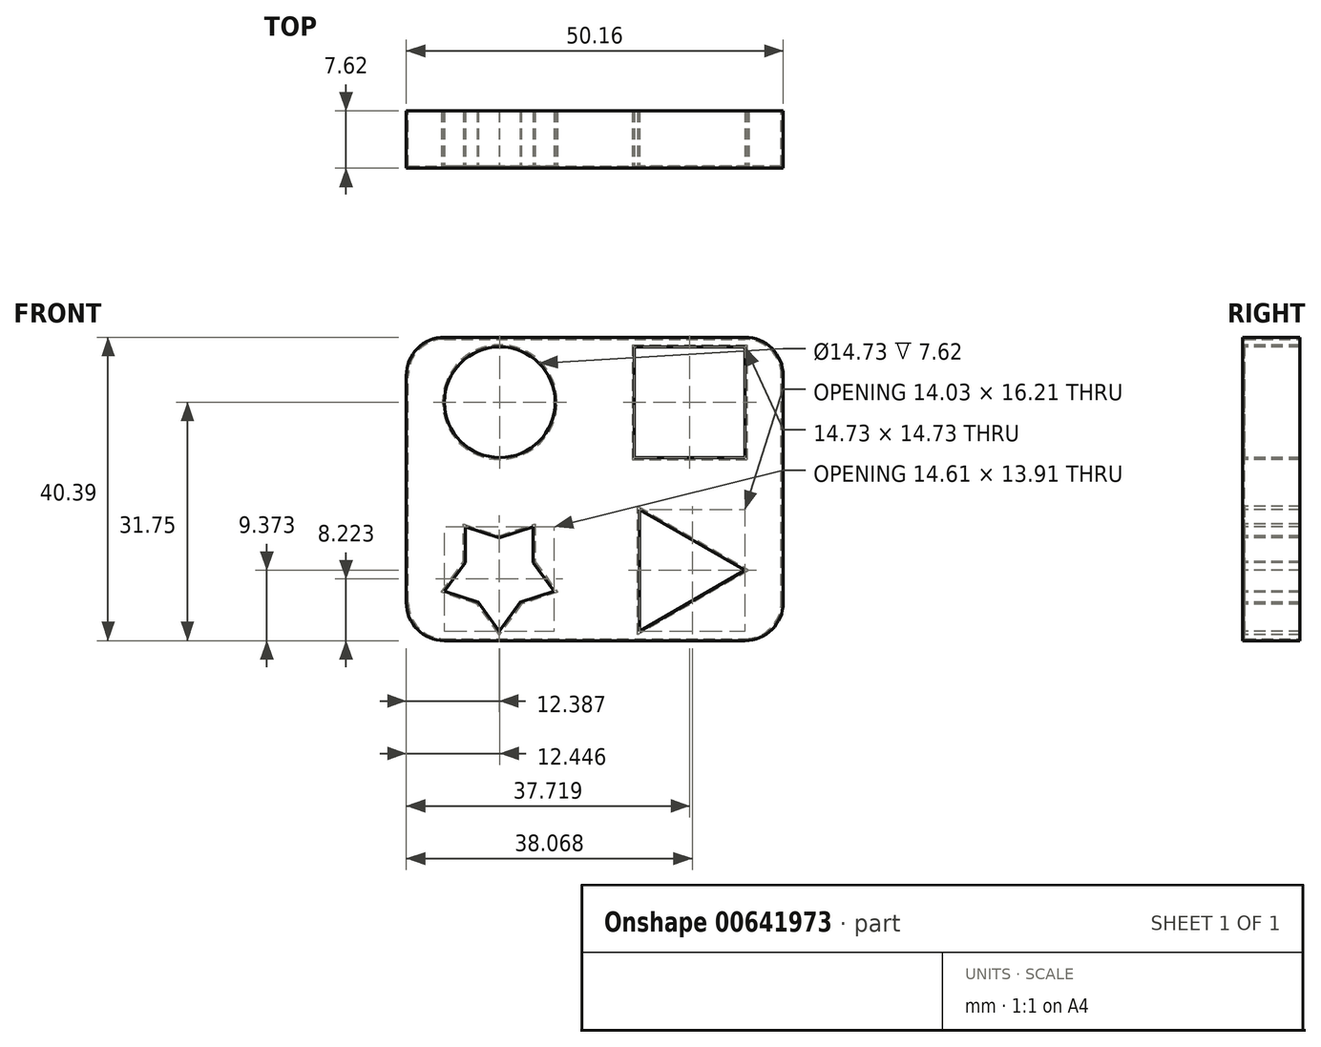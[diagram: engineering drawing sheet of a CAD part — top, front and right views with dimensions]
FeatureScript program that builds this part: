
annotation { "Feature Type Name" : "Feature", "Feature Type Description" : "" }
export const myFeature = defineFeature(function(context is Context, id is Id, definition is map)
    precondition{}
    {
        {
            var Q0;
            Q0=qCreatedBy(makeId("Front.planeOp"),FACE);
            var sketch = newSketch(context, id + "F0", { "sketchPlane" : qUnion([Q0])});
            skLineSegment(sketch, "E0.bottom", {"start": v(5.08, 0) * mm, "end": v(45.09, 0) * mm});
            skLineSegment(sketch, "E0.top", {"start": v(5.08, 40.39) * mm, "end": v(45.09, 40.39) * mm});
            skLineSegment(sketch, "E0.left", {"start": v(0, 5.08) * mm, "end": v(0, 35.3) * mm});
            skLineSegment(sketch, "E0.right", {"start": v(50.16, 5.08) * mm, "end": v(50.16, 35.3) * mm});
            skPoint(sketch, "E1.visualSharp", {"position": v(50.16, 40.39) * mm});
            skArc(sketch, "E1.filletArc", {"start": v(50.16, 35.3) * mm, "mid": v(48.68, 38.9) * mm, "end": v(45.09, 40.39) * mm});
            skPoint(sketch, "E2.visualSharp", {"position": v(0, 40.39) * mm});
            skArc(sketch, "E2.filletArc", {"start": v(5.08, 40.39) * mm, "mid": v(1.49, 38.9) * mm, "end": v(0, 35.3) * mm});
            skPoint(sketch, "E3.visualSharp", {"position": v(0, 0) * mm});
            skArc(sketch, "E3.filletArc", {"start": v(0, 5.08) * mm, "mid": v(1.49, 1.49) * mm, "end": v(5.08, 0) * mm});
            skPoint(sketch, "E4.visualSharp", {"position": v(50.17, 0) * mm});
            skArc(sketch, "E4.filletArc", {"start": v(45.09, 0) * mm, "mid": v(48.68, 1.49) * mm, "end": v(50.16, 5.08) * mm});
            skSolve(sketch);
        }
        {
            var Q0;
            Q0=makeQuery(id+"F0.imprint","IMPRINT",FACE,{"disambiguationData":[TD([[makeQuery(id+"F0.imprint","IMPRINT",EDGE,{"derivedFrom":sQuery(id+"F0.wireOp",EDGE,"E0.bottom")}),1.0]])]});
            extrude(context, id + "F1", {"entities" : qUnion([Q0]), "depth" : 7.62 * mm, "offsetDistance" : 25.4 * mm});
        }
        {
            var Q0;
            Q0=makeQuery(id+"F1.opExtrude","CAP_FACE",FACE,{"disambiguationData":[OSD([sQuery(id+"F0.wireOp",EDGE,"E0.bottom"),sQuery(id+"F0.wireOp",EDGE,"E0.top"),sQuery(id+"F0.wireOp",EDGE,"E0.left"),sQuery(id+"F0.wireOp",EDGE,"E0.right"),sQuery(id+"F0.wireOp",EDGE,"E1.filletArc"),sQuery(id+"F0.wireOp",EDGE,"E2.filletArc"),sQuery(id+"F0.wireOp",EDGE,"E3.filletArc"),sQuery(id+"F0.wireOp",EDGE,"E4.filletArc")])],"isStart":false});
            var sketch = newSketch(context, id + "F2", { "sketchPlane" : qUnion([Q0])});
            skLineSegment(sketch, "E5.bottom", {"start": v(30.35, 39.12) * mm, "end": v(45.09, 39.12) * mm});
            skLineSegment(sketch, "E5.top", {"start": v(30.35, 24.38) * mm, "end": v(45.09, 24.38) * mm});
            skLineSegment(sketch, "E5.left", {"start": v(30.35, 39.12) * mm, "end": v(30.35, 24.38) * mm});
            skLineSegment(sketch, "E5.right", {"start": v(45.09, 39.12) * mm, "end": v(45.09, 24.38) * mm});
            skSolve(sketch);
        }
        {
            var Q0;
            Q0=makeQuery(id+"F2.imprint","IMPRINT",FACE,{"disambiguationData":[TD([[makeQuery(id+"F2.imprint","IMPRINT",EDGE,{"derivedFrom":sQuery(id+"F2.wireOp",EDGE,"E5.bottom")}),1.0]])]});
            var sketch = newSketch(context, id + "F3", { "sketchPlane" : qUnion([Q0])});
            skLineSegment(sketch, "E6", {"start": v(31.05, 1.27) * mm, "end": v(31.05, 17.48) * mm});
            skLineSegment(sketch, "E7", {"start": v(31.05, 17.48) * mm, "end": v(45.09, 9.37) * mm});
            skLineSegment(sketch, "E8", {"start": v(45.09, 9.37) * mm, "end": v(31.05, 1.27) * mm});
            skSolve(sketch);
        }
        {
            var Q0;
            Q0=makeQuery(id+"F2.imprint","IMPRINT",FACE,{"disambiguationData":[TD([[makeQuery(id+"F2.imprint","IMPRINT",EDGE,{"derivedFrom":sQuery(id+"F2.wireOp",EDGE,"E5.bottom")}),1.0]])]});
            var sketch = newSketch(context, id + "F4", { "sketchPlane" : qUnion([Q0])});
            skCircle(sketch, "E9.cCircle", {"center": v(12.38, 8.95) * mm, "radius": 7.68 * mm, "construction": true});
            skLineSegment(sketch, "E9.0", {"start": v(12.4, 1.27) * mm, "end": v(5.08, 6.57) * mm});
            skLineSegment(sketch, "E9.1", {"start": v(5.08, 6.57) * mm, "end": v(7.86, 15.16) * mm});
            skLineSegment(sketch, "E9.2", {"start": v(7.86, 15.16) * mm, "end": v(16.9, 15.18) * mm});
            skLineSegment(sketch, "E9.3", {"start": v(16.9, 15.18) * mm, "end": v(19.7, 6.59) * mm});
            skLineSegment(sketch, "E9.4", {"start": v(19.7, 6.59) * mm, "end": v(12.4, 1.27) * mm});
            skLineSegment(sketch, "E10", {"start": v(16.9, 15.18) * mm, "end": v(16.9, 10.43) * mm});
            skLineSegment(sketch, "E11", {"start": v(16.9, 10.43) * mm, "end": v(19.7, 6.59) * mm});
            skLineSegment(sketch, "E12", {"start": v(19.7, 6.59) * mm, "end": v(15.16, 5.1) * mm});
            skLineSegment(sketch, "E13", {"start": v(15.16, 5.1) * mm, "end": v(12.4, 1.27) * mm});
            skLineSegment(sketch, "E14", {"start": v(12.4, 1.27) * mm, "end": v(9.6, 5.1) * mm});
            skLineSegment(sketch, "E15", {"start": v(9.6, 5.1) * mm, "end": v(5.08, 6.57) * mm});
            skLineSegment(sketch, "E16", {"start": v(5.08, 6.57) * mm, "end": v(7.87, 10.41) * mm});
            skLineSegment(sketch, "E17", {"start": v(7.87, 10.41) * mm, "end": v(7.86, 15.16) * mm});
            skLineSegment(sketch, "E18", {"start": v(7.86, 15.16) * mm, "end": v(12.38, 13.7) * mm});
            skLineSegment(sketch, "E19", {"start": v(12.38, 13.7) * mm, "end": v(16.9, 15.18) * mm});
            skSolve(sketch);
        }
        {
            var Q0;
            Q0=makeQuery(id+"F2.imprint","IMPRINT",FACE,{"disambiguationData":[TD([[makeQuery(id+"F2.imprint","IMPRINT",EDGE,{"derivedFrom":sQuery(id+"F2.wireOp",EDGE,"E5.bottom")}),-1.0]])]});
            extrude(context, id + "F5", {"entities" : qUnion([Q0]), "operationType" : NewBodyOperationType.REMOVE, "oppositeDirection" : true, "depth" : 25.4 * mm, "offsetDistance" : 25.4 * mm});
        }
        {
            var Q0;
            Q0=makeQuery(id+"F3.imprint","IMPRINT",FACE,{"disambiguationData":[TD([[makeQuery(id+"F3.imprint","IMPRINT",EDGE,{"derivedFrom":sQuery(id+"F3.wireOp",EDGE,"E6")}),-1.0]])]});
            extrude(context, id + "F6", {"entities" : qUnion([Q0]), "operationType" : NewBodyOperationType.REMOVE, "oppositeDirection" : true, "depth" : 25.4 * mm, "offsetDistance" : 25.4 * mm});
        }
        {
            var Q0;
            Q0=makeQuery(id+"F4.imprint","IMPRINT",FACE,{"disambiguationData":[TD([[makeQuery(id+"F4.imprint","IMPRINT",EDGE,{"derivedFrom":sQuery(id+"F4.wireOp",EDGE,"E10")}),-1.0]])]});
            extrude(context, id + "F7", {"entities" : qUnion([Q0]), "operationType" : NewBodyOperationType.REMOVE, "oppositeDirection" : true, "depth" : 25.4 * mm, "offsetDistance" : 25.4 * mm});
        }
        {
            var Q0;
            Q0=makeQuery(id+"F1.opExtrude","CAP_FACE",FACE,{"disambiguationData":[OSD([sQuery(id+"F0.wireOp",EDGE,"E0.bottom"),sQuery(id+"F0.wireOp",EDGE,"E0.top"),sQuery(id+"F0.wireOp",EDGE,"E0.left"),sQuery(id+"F0.wireOp",EDGE,"E0.right"),sQuery(id+"F0.wireOp",EDGE,"E1.filletArc"),sQuery(id+"F0.wireOp",EDGE,"E2.filletArc"),sQuery(id+"F0.wireOp",EDGE,"E3.filletArc"),sQuery(id+"F0.wireOp",EDGE,"E4.filletArc")])],"isStart":false});
            var sketch = newSketch(context, id + "F8", { "sketchPlane" : qUnion([Q0])});
            skCircle(sketch, "E20", {"center": v(12.45, 31.75) * mm, "radius": 7.37 * mm});
            skSolve(sketch);
        }
        {
            var Q0;
            Q0=makeQuery(id+"F8.imprint","IMPRINT",FACE,{"disambiguationData":[TD([[makeQuery(id+"F8.imprint","IMPRINT",EDGE,{"derivedFrom":sQuery(id+"F8.wireOp",EDGE,"E20")}),1.0]])]});
            extrude(context, id + "F9", {"entities" : qUnion([Q0]), "operationType" : NewBodyOperationType.REMOVE, "oppositeDirection" : true, "depth" : 25.4 * mm, "offsetDistance" : 25.4 * mm});
        }
        {
            var Q0;
            Q0=makeQuery(id+"F1.opExtrude","CAP_FACE",FACE,{"disambiguationData":[OSD([sQuery(id+"F0.wireOp",EDGE,"E0.bottom"),sQuery(id+"F0.wireOp",EDGE,"E0.top"),sQuery(id+"F0.wireOp",EDGE,"E0.left"),sQuery(id+"F0.wireOp",EDGE,"E0.right"),sQuery(id+"F0.wireOp",EDGE,"E1.filletArc"),sQuery(id+"F0.wireOp",EDGE,"E2.filletArc"),sQuery(id+"F0.wireOp",EDGE,"E3.filletArc"),sQuery(id+"F0.wireOp",EDGE,"E4.filletArc")])],"isStart":true});
            shell(context, id + "F10", {"entities" : qUnion([Q0]), "thickness" : 0.25 * mm});
        }
    });
